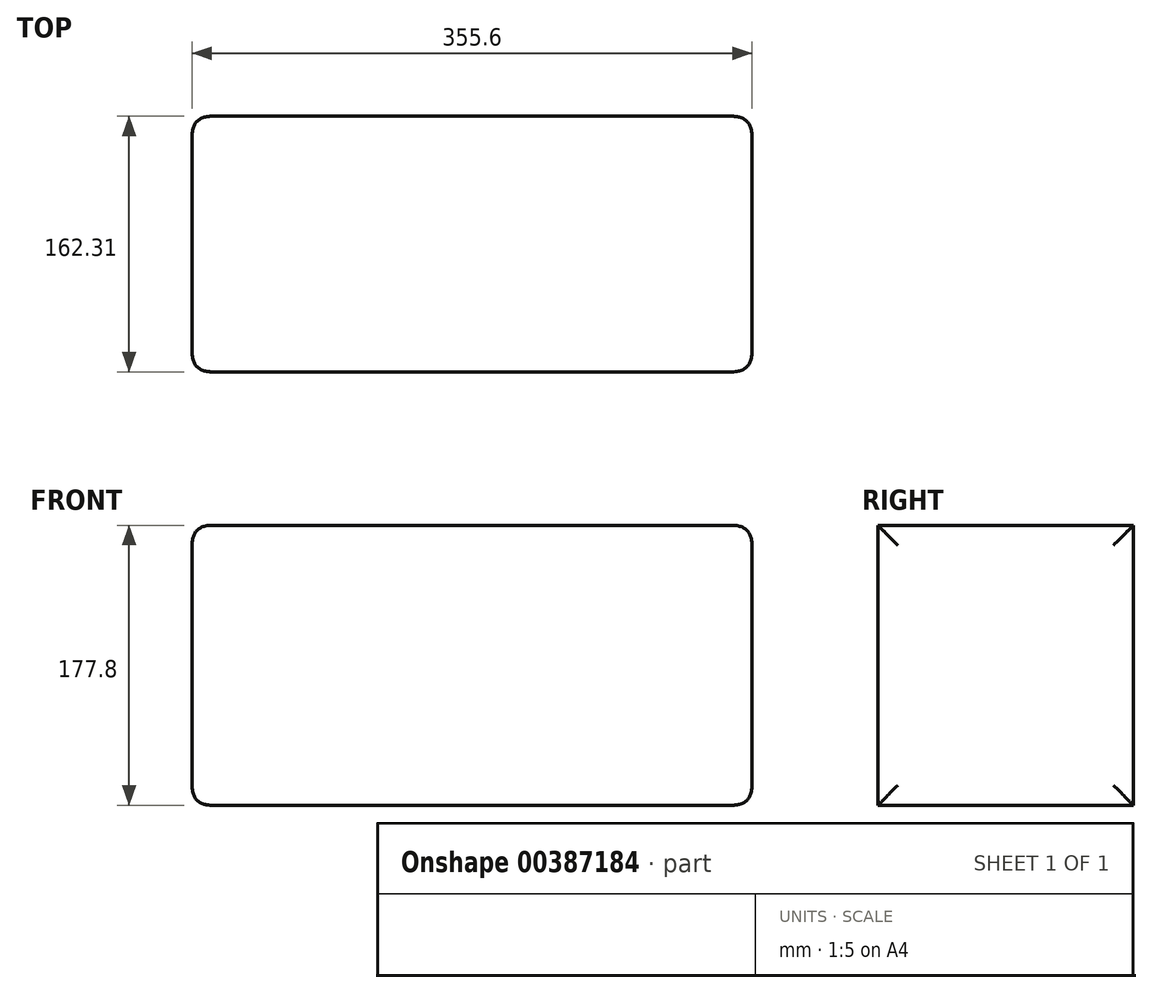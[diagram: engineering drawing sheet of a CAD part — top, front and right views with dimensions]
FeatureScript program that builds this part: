
annotation { "Feature Type Name" : "Feature", "Feature Type Description" : "" }
export const myFeature = defineFeature(function(context is Context, id is Id, definition is map)
    precondition{}
    {
        {
            var Q0;
            Q0=qCreatedBy(makeId("Front.planeOp"),FACE);
            var sketch = newSketch(context, id + "F0", { "sketchPlane" : qUnion([Q0])});
            skLineSegment(sketch, "E0.bottom", {"start": v(177.8, 88.9) * mm, "end": v(-177.8, 88.9) * mm});
            skLineSegment(sketch, "E0.top", {"start": v(177.8, -88.9) * mm, "end": v(-177.8, -88.9) * mm});
            skLineSegment(sketch, "E0.left", {"start": v(177.8, 88.9) * mm, "end": v(177.8, -88.9) * mm});
            skLineSegment(sketch, "E0.right", {"start": v(-177.8, 88.9) * mm, "end": v(-177.8, -88.9) * mm});
            skPoint(sketch, "E0.middle", {"position": v(0, 0) * mm});
            skLineSegment(sketch, "E1.bottom", {"start": v(-177.8, 88.9) * mm, "end": v(177.8, 88.9) * mm});
            skLineSegment(sketch, "E1.top", {"start": v(-177.8, -88.9) * mm, "end": v(177.8, -88.9) * mm});
            skSolve(sketch);
        }
        {
            var Q0;
            Q0 = qSketchRegion(id + "F0", true);
            extrude(context, id + "F1", {"entities" : qUnion([Q0]), "depth" : 162.3 * mm});
        }
        {
            var Q0;
            Q0=makeQuery(id+"F1.opExtrude","CAP_EDGE",EDGE,{"disambiguationData":[OSD([sQuery(id+"F0.wireOp",EDGE,"E1.bottom")])],"isStart":false});
            var Q1;
            Q1=makeQuery(id+"F1.opExtrude","CAP_EDGE",EDGE,{"disambiguationData":[OSD([sQuery(id+"F0.wireOp",EDGE,"E0.right")])],"isStart":false});
            var Q2;
            Q2=makeQuery(id+"F1.opExtrude","CAP_EDGE",EDGE,{"disambiguationData":[OSD([sQuery(id+"F0.wireOp",EDGE,"E0.left")])],"isStart":false});
            var Q3;
            Q3=makeQuery(id+"F1.opExtrude","CAP_EDGE",EDGE,{"disambiguationData":[OSD([sQuery(id+"F0.wireOp",EDGE,"E0.right")])],"isStart":true});
            var Q4;
            Q4=makeQuery(id+"F1.opExtrude","CAP_EDGE",EDGE,{"disambiguationData":[OSD([sQuery(id+"F0.wireOp",EDGE,"E0.left")])],"isStart":true});
            var Q5;
            Q5=makeQuery(id+"F1.opExtrude","SWEPT_FACE",FACE,{"disambiguationData":[OSD([sQuery(id+"F0.wireOp",EDGE,"E0.right")])]});
            var Q6;
            Q6=makeQuery(id+"F1.opExtrude","SWEPT_EDGE",EDGE,{"disambiguationData":[OSD([sQuery(id+"F0.wireOp",EDGE,"E1.bottom"),sQuery(id+"F0.wireOp",EDGE,"E0.left")])]});
            var Q7;
            Q7=makeQuery(id+"F1.opExtrude","CAP_EDGE",EDGE,{"disambiguationData":[OSD([sQuery(id+"F0.wireOp",EDGE,"E1.bottom")])],"isStart":true});
            fillet(context, id + "F2", {"entities" : qUnion([Q0, Q1, Q2, Q3, Q4, Q5, Q6, Q7]), "radius" : 12.7 * mm, "tangentPropagation" : true, "rho" : 0.5, "crossSection" : FilletCrossSection.CONIC, "allowEdgeOverflow" : false});
        }
    });
